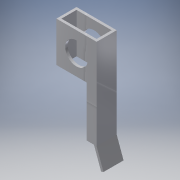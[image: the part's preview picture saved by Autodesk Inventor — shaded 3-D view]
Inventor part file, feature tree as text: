
AUTODESK INVENTOR PART (.ipt)
format: ipt  version: 2016 (Build 200138000, 138)  size: 139,776 bytes
history: native  units: in
note: dims shown in document units (in); Inventor stores cm internally (conversion verified against a paired STEP export)
features: extrude x4, sketch x4
ambient origin geometry x8: Origin, YZ Plane, XZ Plane, XY Plane, X Axis, Y Axis, Z Axis, Center Point
bodies: Solid1 (feature_tree)
feature tree (8):
  extrude  "Extrusion1"  Depth=1.0in
  extrude  "Extrusion2"  Depth=4.5in TaperAngle=0.0deg
  extrude  "Extrusion3"  Depth=2.5in
  extrude  "Extrusion4"  Depth=1.0in
  sketch  "Sketch1"  dims[d0=2.0in d1=1.0in]
  sketch  "Sketch2"  dims[d2=0.125in d3=4.5in d4=0.0in]
  sketch  "Sketch3"  dims[d5=1.5in d6=2.5in]
  sketch  "Sketch4"  dims[d7=1.0in d8=0.0in d9=1.125in d10=1.0in d11=1.0in d12=1.0in d13=0.0in d14=1.0in d15=0.125in d16=0.7559in d17=1.0in d18=0.0in]
